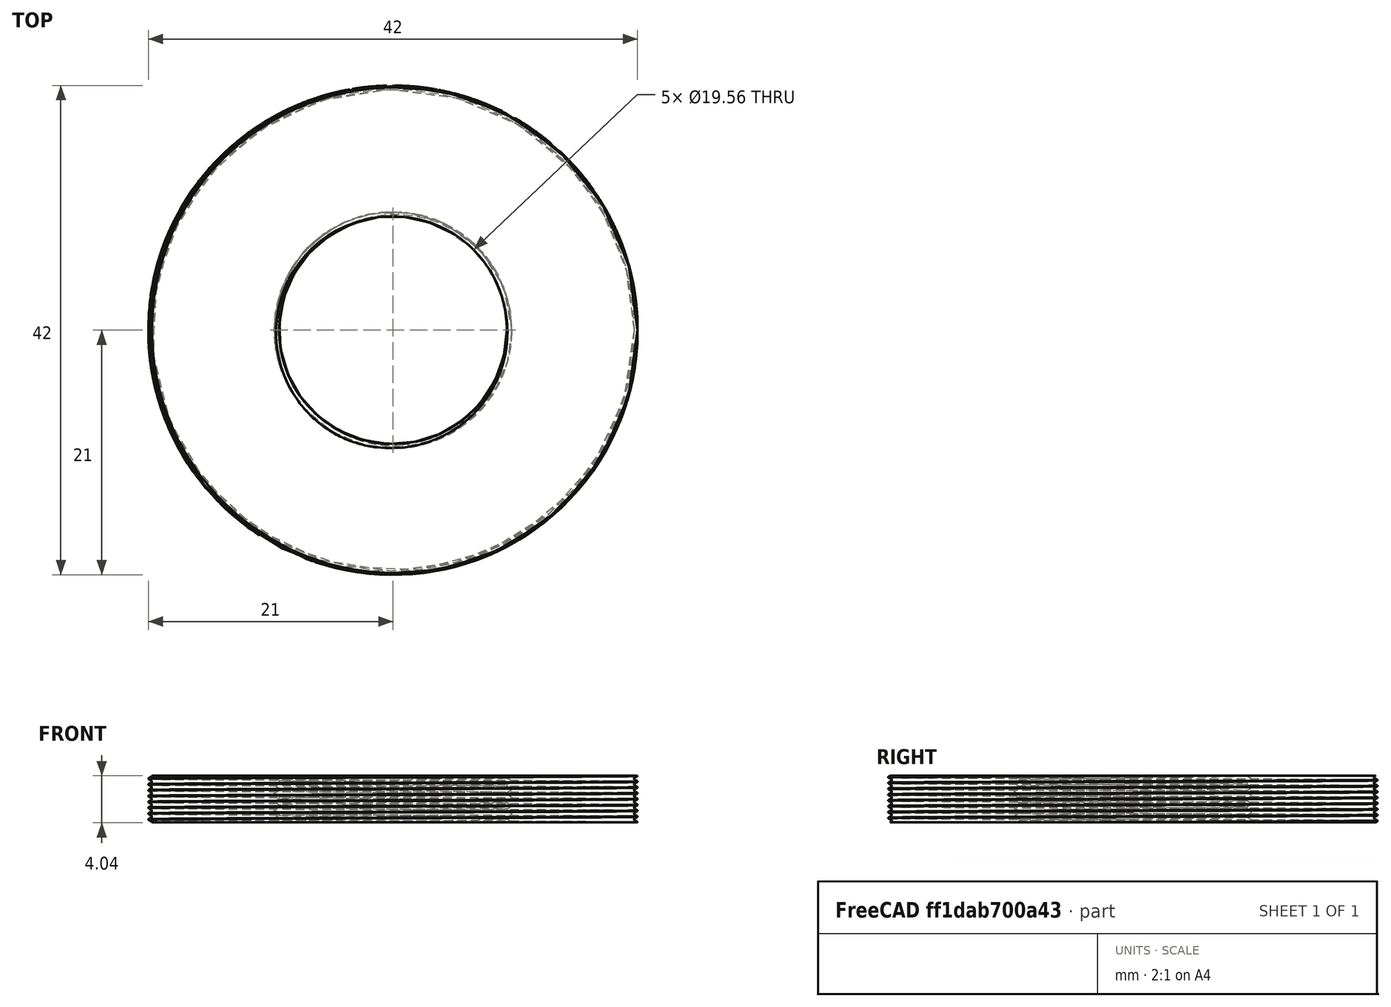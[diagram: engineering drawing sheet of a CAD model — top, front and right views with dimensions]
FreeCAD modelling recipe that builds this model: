
FCSTD DOCUMENT  (FreeCAD 0.22R0.21.2)
Label: RMS_to_M42x05
License: All rights reserved
LicenseURL: http://en.wikipedia.org/wiki/All_rights_reserved
objects: Part::Cut×3, Part::Cylinder×2, Part::FeaturePython×2, Part::Feature×1
note: 8 computed .brp shape members not serialized (recipe doc carries the construction recipe); baked Part::Feature solids carry a one-line shape summary decoded from their .brp

FEATURE [Part::Cylinder] Cylinder
  Angle = 360
  AttacherType = Attacher::AttachEngine3D
  FirstAngle = 0
  Height = 4
  Radius = 21
  SecondAngle = 0
FEATURE [Part::FeaturePython] ScrewDie  label="42x8-ScrewDie_M42x0_5"  # WARN: FeaturePython — macro-defined, semantics opaque (R4)
  Diameter = 29
  DiameterCustom = 42
  Invert = false
  LeftHanded = false
  Length = 8
  MatchOuter = false
  PitchCustom = 0.5
  Placement = pos=(0,0,6) rot=(0,0,1;0rad)
  Thread = true
  Type = 0
FEATURE [Part::Cylinder] Cylinder001
  Angle = 360
  AttacherType = Attacher::AttachEngine3D
  FirstAngle = 0
  Height = 10
  Radius = 9.708
  SecondAngle = 0
FEATURE [Part::Cut] Cut
  Base = -> Cylinder
  Tool = -> Cylinder001
FEATURE [Part::FeaturePython] ScrewTap  label="20.32x8-ScrewTap_RMS"  # WARN: FeaturePython — macro-defined, semantics opaque (R4)
  Diameter = 33
  DiameterCustom = 20.32
  Invert = false
  LeftHanded = false
  Length = 8
  MatchOuter = false
  PitchCustom = 0.705612
  Placement = pos=(0,0,6) rot=(0,0,1;0rad)
  Thread = true
  Type = 3
FEATURE [Part::Cut] Cut001
  Base = -> Cut
  Tool = -> ScrewTap
FEATURE [Part::Cut] Cut002  label="RMStoM42x0_5Adapter"
  Base = -> Cut001
  Tool = -> ScrewDie
FEATURE [Part::Feature] Cut002_solid  label="RMStoM42x0_5Adapter (Solid)"
  shape: bbox 54.87 x 61.55 x 5.645 mm, 67 faces (baked)
